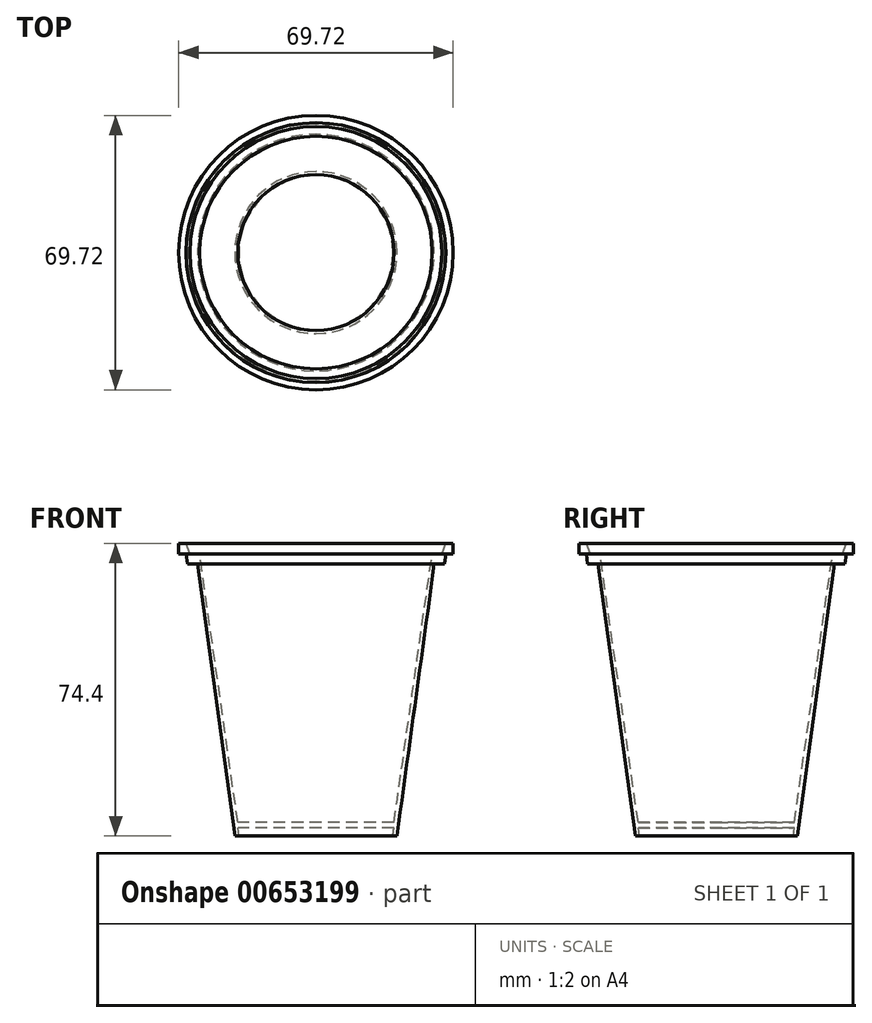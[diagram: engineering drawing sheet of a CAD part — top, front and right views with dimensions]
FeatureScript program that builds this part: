
annotation { "Feature Type Name" : "Feature", "Feature Type Description" : "" }
export const myFeature = defineFeature(function(context is Context, id is Id, definition is map)
    precondition{}
    {
        {
            var Q0;
            Q0=qCreatedBy(makeId("Front.planeOp"),FACE);
            var sketch = newSketch(context, id + "F0", { "sketchPlane" : qUnion([Q0])});
            skLineSegment(sketch, "E0", {"start": v(-30.06, 29) * mm, "end": v(-20.6, -40.12) * mm});
            skLineSegment(sketch, "E1", {"start": v(-32.67, 29) * mm, "end": v(-30.06, 29) * mm});
            skLineSegment(sketch, "E2", {"start": v(-32.67, 29) * mm, "end": v(-33, 31.45) * mm});
            skLineSegment(sketch, "E3", {"start": v(-33, 31.45) * mm, "end": v(-34.86, 31.45) * mm});
            skLineSegment(sketch, "E4", {"start": v(-34.86, 31.45) * mm, "end": v(-34.86, 34.22) * mm});
            skLineSegment(sketch, "E5", {"start": v(-18.57, -36.73) * mm, "end": v(0, -36.73) * mm});
            skLineSegment(sketch, "E6", {"start": v(0, -36.73) * mm, "end": v(0, -38.13) * mm});
            skLineSegment(sketch, "E7", {"start": v(0, -38.13) * mm, "end": v(-19.83, -38.13) * mm});
            skLineSegment(sketch, "E8", {"start": v(-19.83, -38.13) * mm, "end": v(-19.55, -40.18) * mm});
            skLineSegment(sketch, "E9", {"start": v(-19.55, -40.18) * mm, "end": v(-20.6, -40.12) * mm});
            skLineSegment(sketch, "E10", {"start": v(-34.86, 34.22) * mm, "end": v(-33, 34.22) * mm});
            skLineSegment(sketch, "E11", {"start": v(-33, 34.22) * mm, "end": v(-32, 31.45) * mm});
            skLineSegment(sketch, "E12", {"start": v(-32, 31.45) * mm, "end": v(-29.54, 31.45) * mm});
            skLineSegment(sketch, "E13", {"start": v(-29.54, 31.45) * mm, "end": v(-19.83, -36.73) * mm});
            skLineSegment(sketch, "E14", {"start": v(-19.83, -36.73) * mm, "end": v(-18.57, -36.73) * mm});
            skSolve(sketch);
        }
        {
            var Q0;
            Q0=qCreatedBy(makeId("Front.planeOp"),FACE);
            var sketch = newSketch(context, id + "F1", { "sketchPlane" : qUnion([Q0])});
            skLineSegment(sketch, "E15", {"start": v(0, 52.67) * mm, "end": v(0, -63.8) * mm});
            skSolve(sketch);
        }
        {
            var Q0;
            Q0=makeQuery(id+"F0.imprint","IMPRINT",FACE,{"disambiguationData":[TD([[makeQuery(id+"F0.imprint","IMPRINT",EDGE,{"derivedFrom":sQuery(id+"F0.wireOp",EDGE,"E0")}),1.0]])]});
            var Q1;
            Q1=sQuery(id+"F1.wireOp",EDGE,"E15");
            revolve(context, id + "F2", {"entities" : qUnion([Q0]), "axis" : qUnion([Q1]), "revolveType" : RevolveType.FULL});
        }
    });
